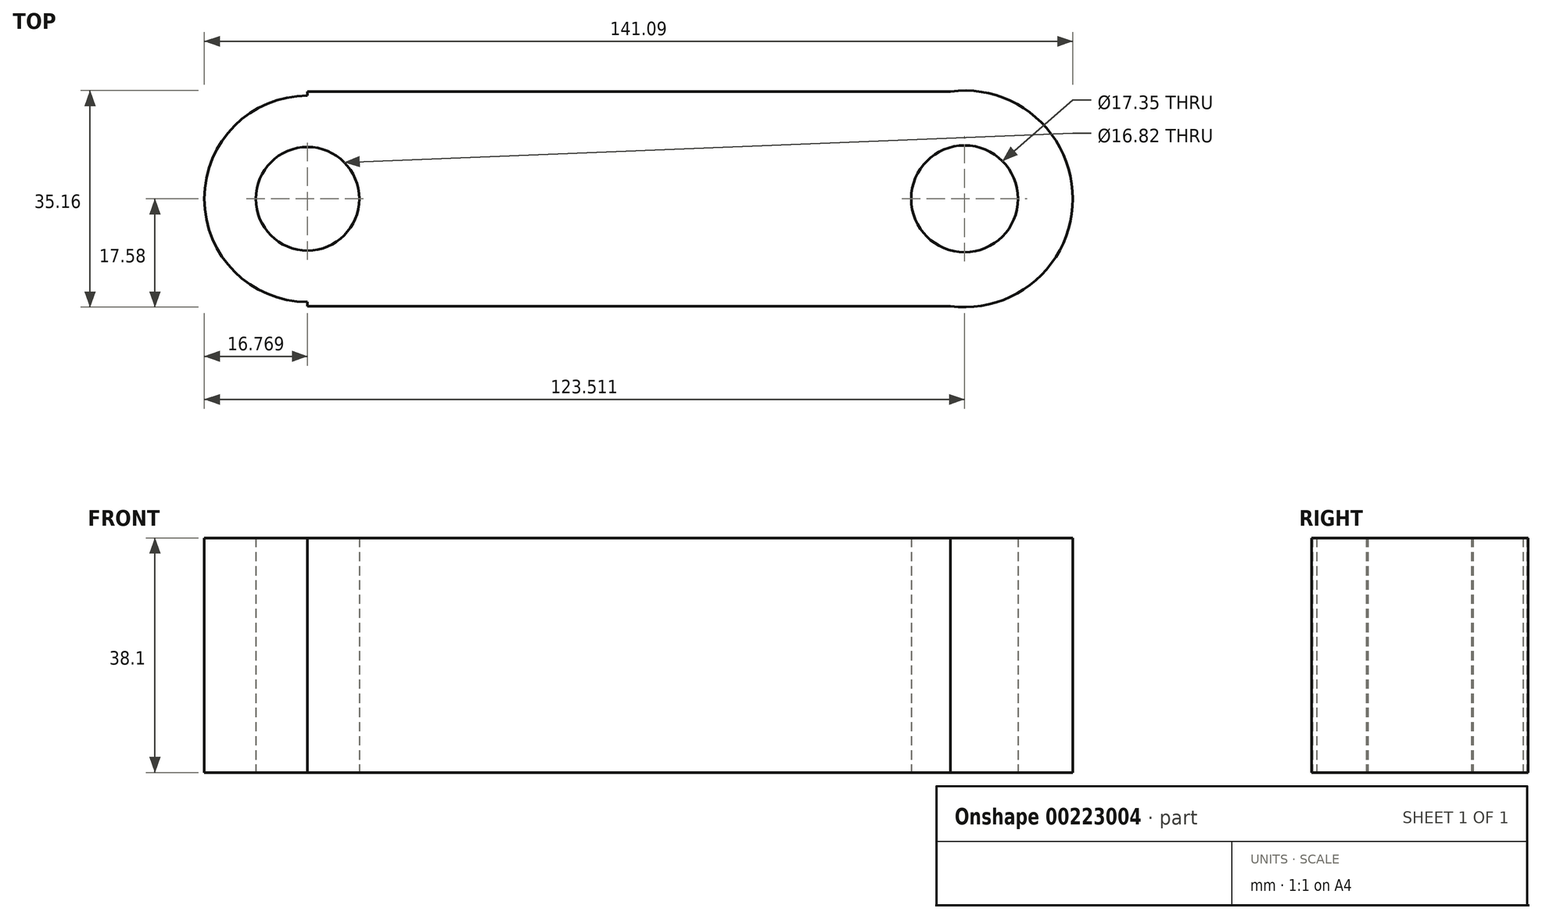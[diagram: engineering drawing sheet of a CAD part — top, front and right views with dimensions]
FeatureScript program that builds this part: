
annotation { "Feature Type Name" : "Feature", "Feature Type Description" : "" }
export const myFeature = defineFeature(function(context is Context, id is Id, definition is map)
    precondition{}
    {
        {
            var Q0;
            Q0=qCreatedBy(makeId("Top.planeOp"),FACE);
            var sketch = newSketch(context, id + "F0", { "sketchPlane" : qUnion([Q0])});
            skLineSegment(sketch, "E0.bottom", {"start": v(53.37, 17.43) * mm, "end": v(-53.37, 17.43) * mm});
            skLineSegment(sketch, "E0.top", {"start": v(53.37, -17.43) * mm, "end": v(-53.37, -17.43) * mm});
            skLineSegment(sketch, "E0.right", {"start": v(-53.37, 17.43) * mm, "end": v(-53.37, 16.77) * mm});
            skPoint(sketch, "E0.middle", {"position": v(0, 0) * mm});
            skArc(sketch, "E1", {"start": v(51.08, -17.43) * mm, "mid": v(70.95, 0) * mm, "end": v(51.08, 17.43) * mm});
            skCircle(sketch, "E2", {"center": v(53.37, 0) * mm, "radius": 8.67 * mm});
            skCircle(sketch, "E3", {"center": v(-53.37, 0) * mm, "radius": 16.77 * mm});
            skCircle(sketch, "E4", {"center": v(-53.37, 0) * mm, "radius": 8.4 * mm});
            skLineSegment(sketch, "E5.trimOffspring", {"start": v(-53.37, -16.77) * mm, "end": v(-53.37, -17.43) * mm});
            skSolve(sketch);
        }
        {
            var Q0;
            {var subQ1=sQuery(id+"F0.wireOp",EDGE,"E0.right");Q0=makeQuery(id+"F0.imprint","IMPRINT",FACE,{"disambiguationData":[TD([[makeQuery(id+"F0.imprint","IMPRINT",EDGE,{"derivedFrom":subQ1}),1.0]])]});}
            var Q1;
            Q1 = qSketchRegion(id + "FHDRVWFa8T0vLyi_0", true);
            extrude(context, id + "F1", {"entities" : qUnion([Q0, Q1]), "depth" : 25.4 * mm});
        }
        {
            var Q0;
            Q0 = qSketchRegion(id + "F0", true);
            extrude(context, id + "F2", {"entities" : qUnion([Q0]), "operationType" : NewBodyOperationType.ADD, "depth" : 38.1 * mm});
        }
    });
